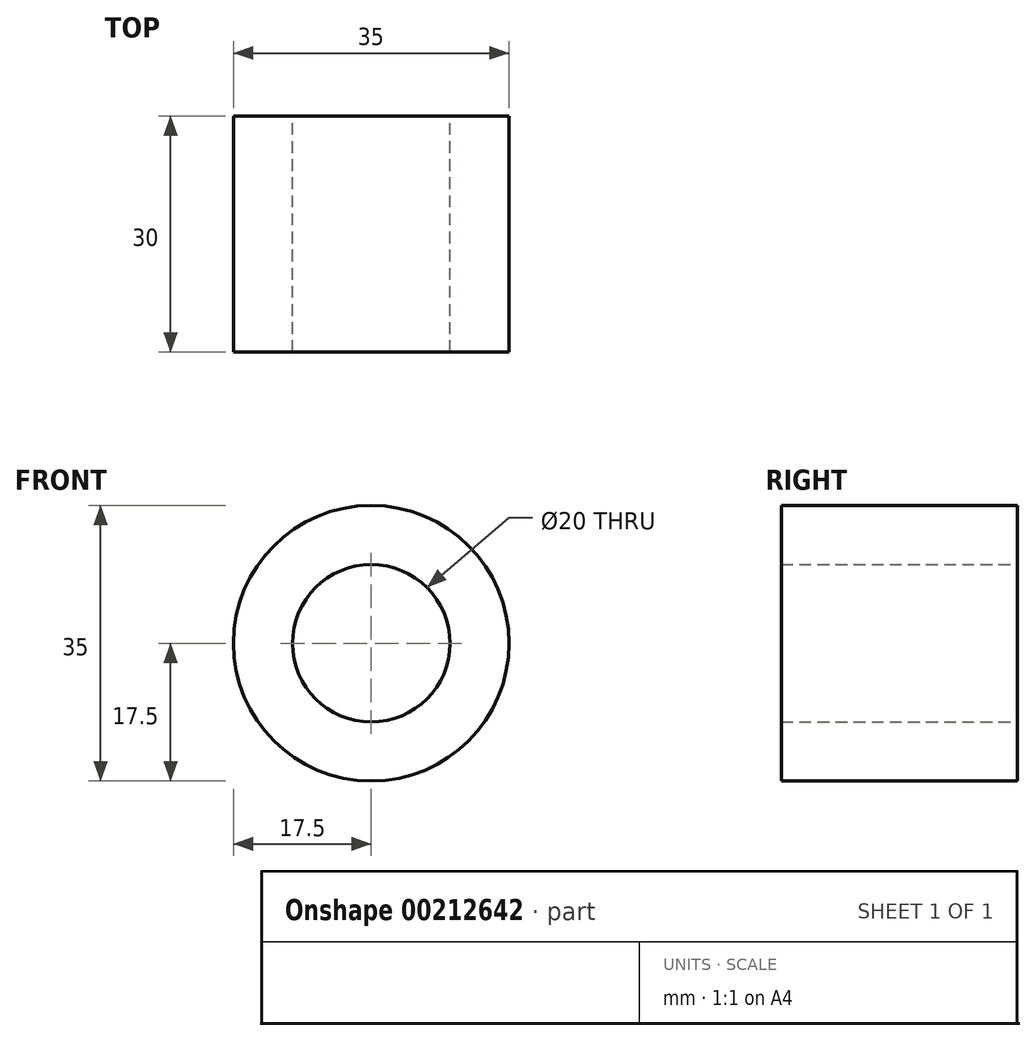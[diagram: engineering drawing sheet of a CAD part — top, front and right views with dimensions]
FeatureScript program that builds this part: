
annotation { "Feature Type Name" : "Feature", "Feature Type Description" : "" }
export const myFeature = defineFeature(function(context is Context, id is Id, definition is map)
    precondition{}
    {
        {
            var Q0;
            Q0=qCreatedBy(makeId("Front.planeOp"),FACE);
            var sketch = newSketch(context, id + "F0", { "sketchPlane" : qUnion([Q0])});
            skCircle(sketch, "E0", {"center": v(0, 0) * mm, "radius": 10 * mm});
            skCircle(sketch, "E1", {"center": v(0, 0) * mm, "radius": 17.5 * mm});
            skSolve(sketch);
        }
        {
            var Q0;
            Q0 = qSketchRegion(id + "F0", true);
            extrude(context, id + "F1", {"entities" : qUnion([Q0]), "depth" : 30 * mm});
        }
    });
